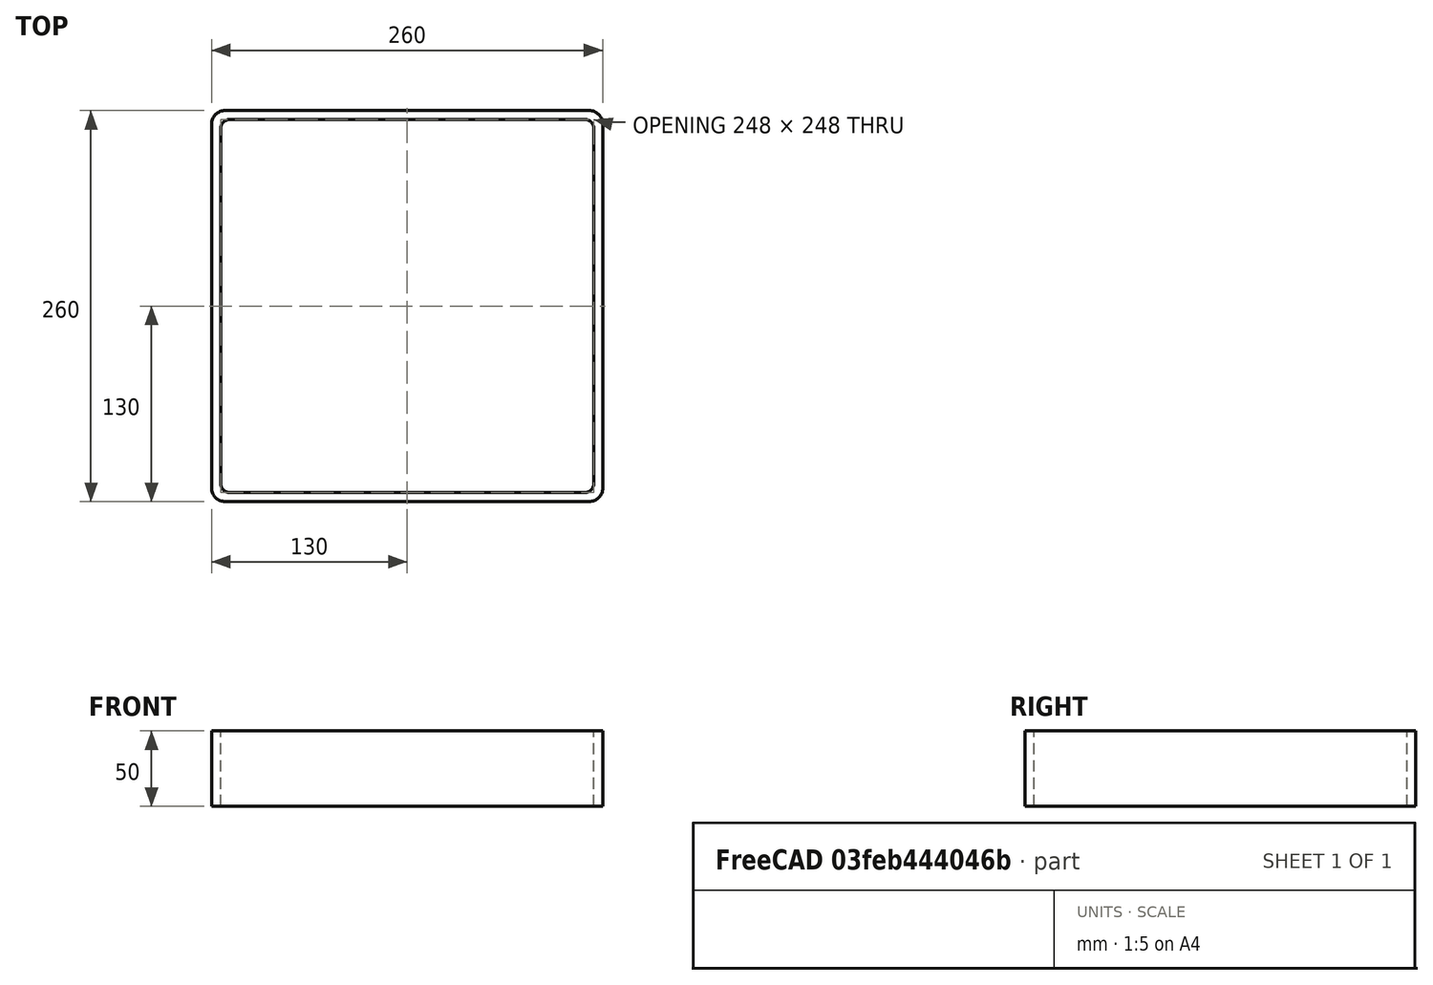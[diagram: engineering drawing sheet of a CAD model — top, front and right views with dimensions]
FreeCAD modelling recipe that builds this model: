
FCSTD DOCUMENT  (FreeCAD 0.15R4671 (Git))
Label: Square hollow section 260x260x6 EN10219 S235JRH
License: All rights reserved
LicenseURL: http://en.wikipedia.org/wiki/All_rights_reserved
objects: Sketcher::SketchObject×1, Part::Extrusion×1
note: 2 computed .brp shape members not serialized (recipe doc carries the construction recipe); baked Part::Feature solids carry a one-line shape summary decoded from their .brp

FEATURE [Sketcher::SketchObject] Sketch
  sketch-geometry (16):
    g0: LineSegment StartX=-118 StartY=124 StartZ=0 EndX=118 EndY=124 EndZ=0
    g1: LineSegment StartX=124 StartY=118 StartZ=0 EndX=124 EndY=-118 EndZ=0
    g2: LineSegment StartX=118 StartY=-124 StartZ=0 EndX=-118 EndY=-124 EndZ=0
    g3: LineSegment StartX=-124 StartY=-118 StartZ=0 EndX=-124 EndY=118 EndZ=0
    g4: LineSegment StartX=-121 StartY=130 StartZ=0 EndX=121 EndY=130 EndZ=0
    g5: LineSegment StartX=130 StartY=121 StartZ=0 EndX=130 EndY=-121 EndZ=0
    g6: LineSegment StartX=121 StartY=-130 StartZ=0 EndX=-121 EndY=-130 EndZ=0
    g7: LineSegment StartX=-130 StartY=-121 StartZ=0 EndX=-130 EndY=121 EndZ=0
    g8: ArcOfCircle CenterX=-118 CenterY=118 CenterZ=0 NormalX=0 NormalY=0 NormalZ=1 Radius=6 StartAngle=1.5708 EndAngle=3.14159
    g9: ArcOfCircle CenterX=118 CenterY=118 CenterZ=0 NormalX=0 NormalY=0 NormalZ=1 Radius=6 StartAngle=0 EndAngle=1.5708
    g10: ArcOfCircle CenterX=118 CenterY=-118 CenterZ=0 NormalX=0 NormalY=0 NormalZ=1 Radius=6 StartAngle=4.71239 EndAngle=6.28319
    g11: ArcOfCircle CenterX=-118 CenterY=-118 CenterZ=0 NormalX=0 NormalY=0 NormalZ=1 Radius=6 StartAngle=3.14159 EndAngle=4.71239
    g12: ArcOfCircle CenterX=121 CenterY=121 CenterZ=0 NormalX=0 NormalY=0 NormalZ=1 Radius=9 StartAngle=0 EndAngle=1.5708
    g13: ArcOfCircle CenterX=121 CenterY=-121 CenterZ=0 NormalX=0 NormalY=0 NormalZ=1 Radius=9 StartAngle=4.71239 EndAngle=6.28319
    g14: ArcOfCircle CenterX=-121 CenterY=-121 CenterZ=0 NormalX=0 NormalY=0 NormalZ=1 Radius=9 StartAngle=3.14159 EndAngle=4.71239
    g15: ArcOfCircle CenterX=-121 CenterY=121 CenterZ=0 NormalX=0 NormalY=0 NormalZ=1 Radius=9 StartAngle=1.5708 EndAngle=3.14159
  constraints (36):
    c: Horizontal(g2)
    c: Vertical(g3)
    c: Horizontal(g6)
    c: Vertical(g7)
    c: Tangent(g3,g8) = 1.5708
    c: Tangent(g0,g8) = 1.5708
    c: Tangent(g0,g9) = 1.5708
    c: Tangent(g1,g9) = 1.5708
    c: Tangent(g1,g10) = 1.5708
    c: Tangent(g2,g10) = 1.5708
    c: Tangent(g2,g11) = 1.5708
    c: Tangent(g3,g11) = 1.5708
    c: Tangent(g4,g12) = 1.5708
    c: Tangent(g5,g12) = 1.5708
    c: Tangent(g5,g13) = 1.5708
    c: Tangent(g6,g13) = 1.5708
    c: Tangent(g6,g14) = 1.5708
    c: Tangent(g7,g14) = 1.5708
    c: Tangent(g7,g15) = 1.5708
    c: Tangent(g4,g15) = 1.5708
    c: Equal(g9,g8)
    c: Equal(g9,g11)
    c: Equal(g9,g10)
    c: Equal(g12,g15)
    c: Equal(g12,g14)
    c: Equal(g12,g13)
    c: Symmetric(g4,g6,g-1)
    c: Symmetric(g7,g5,g-2)
    c: DistanceY(g4,g6) = -260
    c: DistanceX(g7,g5) = 260
    c: Symmetric(g3,g1,g-2)
    c: Symmetric(g0,g2,g-1)
    c: DistanceY(g0,g4) = 6
    c: DistanceX(g5,g1) = -6
    c: Radius(g9) = 6
    c: Radius(g12) = 9
FEATURE [Part::Extrusion] Extrude  label="Square hollow section 260x260x6 EN10219 S235JRH"
  Base = -> Sketch
  Dir = (0,0,50)
  Solid = true
